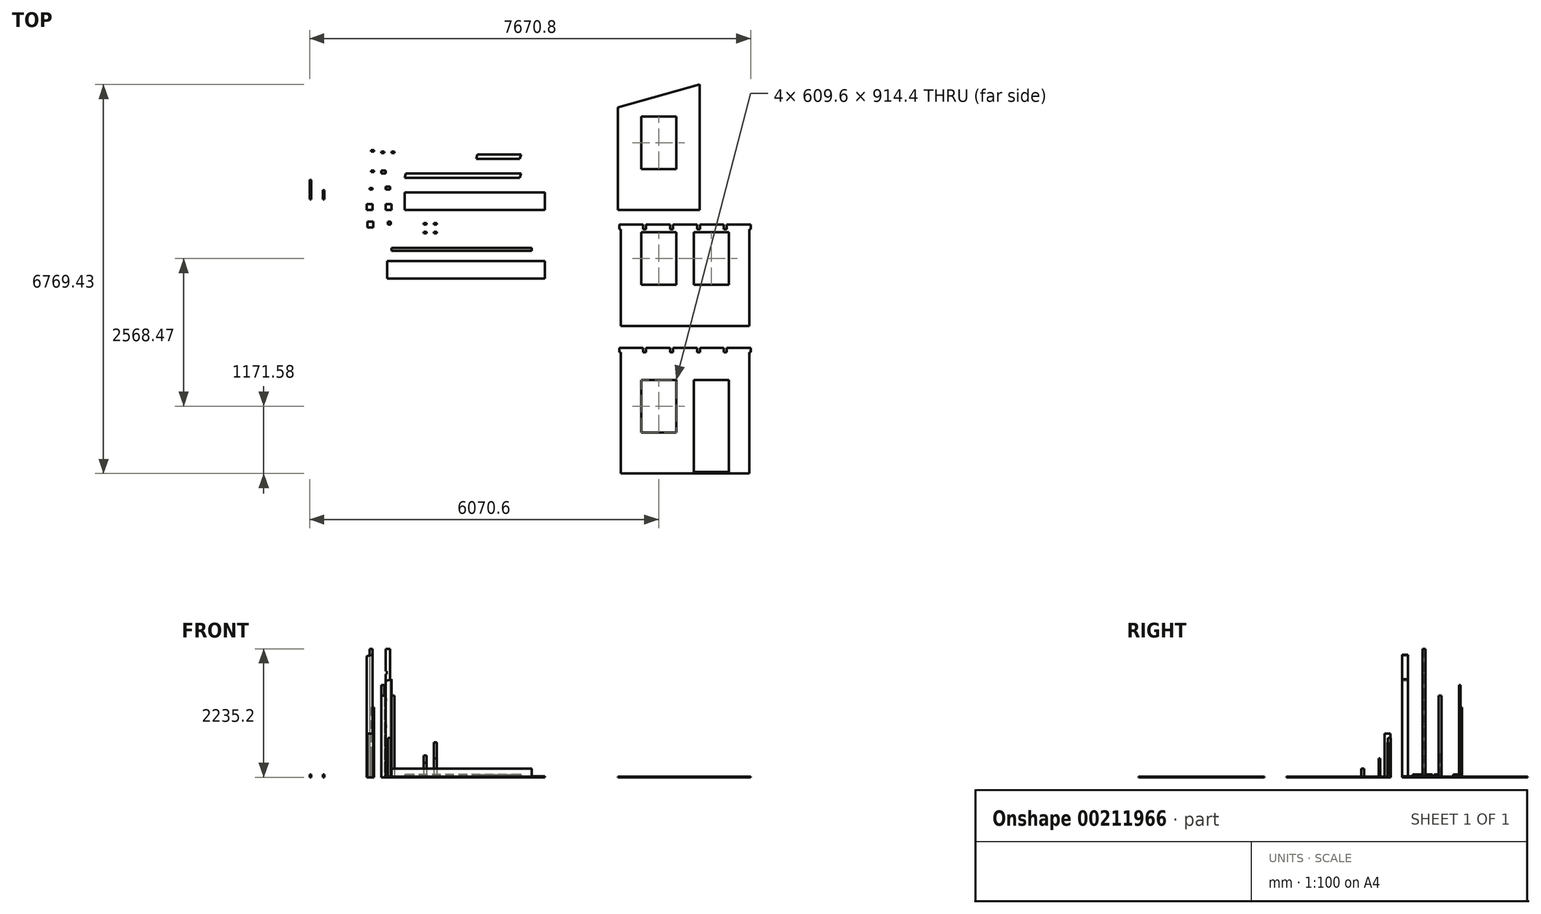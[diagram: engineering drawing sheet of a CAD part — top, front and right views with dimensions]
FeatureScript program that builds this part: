
annotation { "Feature Type Name" : "Feature", "Feature Type Description" : "" }
export const myFeature = defineFeature(function(context is Context, id is Id, definition is map)
    precondition{}
    {
        {
            var Q0;
            Q0=qCreatedBy(makeId("Front.planeOp"),FACE);
            var sketch = newSketch(context, id + "F0", { "sketchPlane" : qUnion([Q0])});
            skLineSegment(sketch, "E0", {"start": v(0, 0) * mm, "end": v(-304.8, 152.4) * mm});
            skLineSegment(sketch, "E1", {"start": v(-304.8, 152.4) * mm, "end": v(-304.8, 203.2) * mm});
            skLineSegment(sketch, "E2", {"start": v(-304.8, 203.2) * mm, "end": v(2133.6, 203.2) * mm});
            skLineSegment(sketch, "E3", {"start": v(2133.6, 203.2) * mm, "end": v(2133.6, 152.4) * mm});
            skLineSegment(sketch, "E4", {"start": v(2133.6, 152.4) * mm, "end": v(1828.8, 0) * mm});
            skLineSegment(sketch, "E5", {"start": v(1828.8, 0) * mm, "end": v(0, 0) * mm});
            skSolve(sketch);
        }
        {
            var Q0;
            Q0=makeQuery(id+"F0.imprint","IMPRINT",FACE,{"disambiguationData":[TD([[makeQuery(id+"F0.imprint","IMPRINT",EDGE,{"derivedFrom":sQuery(id+"F0.wireOp",EDGE,"E0")}),-1.0]])]});
            extrude(context, id + "F1", {"entities" : qUnion([Q0]), "depth" : 152.4 * mm});
        }
        {
            var Q0;
            Q0=qCreatedBy(makeId("Top.planeOp"),FACE);
            var sketch = newSketch(context, id + "F2", { "sketchPlane" : qUnion([Q0])});
            skLineSegment(sketch, "E6.bottom", {"start": v(-736.6, 355.6) * mm, "end": v(-635, 355.6) * mm});
            skLineSegment(sketch, "E6.top", {"start": v(-736.6, 254) * mm, "end": v(-635, 254) * mm});
            skLineSegment(sketch, "E6.left", {"start": v(-736.6, 355.6) * mm, "end": v(-736.6, 254) * mm});
            skLineSegment(sketch, "E6.right", {"start": v(-635, 355.6) * mm, "end": v(-635, 254) * mm});
            skSolve(sketch);
        }
        {
            var Q0;
            Q0=makeQuery(id+"F2.imprint","IMPRINT",FACE,{"disambiguationData":[TD([[makeQuery(id+"F2.imprint","IMPRINT",EDGE,{"derivedFrom":sQuery(id+"F2.wireOp",EDGE,"E6.bottom")}),-1.0]])]});
            extrude(context, id + "F3", {"entities" : qUnion([Q0]), "depth" : 2133.6 * mm});
        }
        {
            var Q0;
            Q0=makeQuery(id+"F3.opExtrude","SWEPT_FACE",FACE,{"disambiguationData":[OSD([sQuery(id+"F2.wireOp",EDGE,"E6.top")])]});
            var sketch = newSketch(context, id + "F4", { "sketchPlane" : qUnion([Q0])});
            skLineSegment(sketch, "E7", {"start": v(-736.6, 2133.6) * mm, "end": v(-736.6, 2105.03) * mm});
            skLineSegment(sketch, "E8", {"start": v(-736.6, 2105.03) * mm, "end": v(-635, 2133.6) * mm});
            skLineSegment(sketch, "E9", {"start": v(-635, 2133.6) * mm, "end": v(-736.6, 2133.6) * mm});
            skSolve(sketch);
        }
        {
            var Q0;
            Q0=makeQuery(id+"F4.imprint","IMPRINT",FACE,{"disambiguationData":[TD([[makeQuery(id+"F4.imprint","IMPRINT",EDGE,{"derivedFrom":sQuery(id+"F4.wireOp",EDGE,"E7")}),1.0]])]});
            extrude(context, id + "F5", {"entities" : qUnion([Q0]), "operationType" : NewBodyOperationType.REMOVE, "endBound" : BoundingType.UP_TO_NEXT, "oppositeDirection" : true, "depth" : 25.4 * mm});
        }
        {
            var Q0;
            Q0=qCreatedBy(makeId("Top.planeOp"),FACE);
            var sketch = newSketch(context, id + "F6", { "sketchPlane" : qUnion([Q0])});
            skLineSegment(sketch, "E10.bottom", {"start": v(-406.4, 355.6) * mm, "end": v(-304.8, 355.6) * mm});
            skLineSegment(sketch, "E10.top", {"start": v(-406.4, 254) * mm, "end": v(-304.8, 254) * mm});
            skLineSegment(sketch, "E10.left", {"start": v(-406.4, 355.6) * mm, "end": v(-406.4, 254) * mm});
            skLineSegment(sketch, "E10.right", {"start": v(-304.8, 355.6) * mm, "end": v(-304.8, 254) * mm});
            skSolve(sketch);
        }
        {
            var Q0;
            Q0=makeQuery(id+"F6.imprint","IMPRINT",FACE,{"disambiguationData":[TD([[makeQuery(id+"F6.imprint","IMPRINT",EDGE,{"derivedFrom":sQuery(id+"F6.wireOp",EDGE,"E10.bottom")}),-1.0]])]});
            extrude(context, id + "F7", {"entities" : qUnion([Q0]), "depth" : 1704.97 * mm});
        }
        {
            var Q0;
            Q0=makeQuery(id+"F7.opExtrude","SWEPT_FACE",FACE,{"disambiguationData":[OSD([sQuery(id+"F6.wireOp",EDGE,"E10.top")])]});
            var sketch = newSketch(context, id + "F8", { "sketchPlane" : qUnion([Q0])});
            skLineSegment(sketch, "E11", {"start": v(-406.4, 1704.98) * mm, "end": v(-406.4, 1676.4) * mm});
            skLineSegment(sketch, "E12", {"start": v(-406.4, 1676.4) * mm, "end": v(-304.8, 1704.98) * mm});
            skLineSegment(sketch, "E13", {"start": v(-304.8, 1704.98) * mm, "end": v(-406.4, 1704.98) * mm});
            skSolve(sketch);
        }
        {
            var Q0;
            Q0=makeQuery(id+"F8.imprint","IMPRINT",FACE,{"disambiguationData":[TD([[makeQuery(id+"F8.imprint","IMPRINT",EDGE,{"derivedFrom":sQuery(id+"F8.wireOp",EDGE,"E11")}),1.0]])]});
            extrude(context, id + "F9", {"entities" : qUnion([Q0]), "operationType" : NewBodyOperationType.REMOVE, "endBound" : BoundingType.UP_TO_NEXT, "oppositeDirection" : true, "depth" : 25.4 * mm});
        }
        {
            var Q0;
            Q0=qCreatedBy(makeId("Top.planeOp"),FACE);
            var sketch = newSketch(context, id + "F10", { "sketchPlane" : qUnion([Q0])});
            skLineSegment(sketch, "E14.bottom", {"start": v(-76.2, 254) * mm, "end": v(2362.2, 254) * mm});
            skLineSegment(sketch, "E14.top", {"start": v(-76.2, 558.8) * mm, "end": v(2362.2, 558.8) * mm});
            skLineSegment(sketch, "E14.left", {"start": v(-76.2, 254) * mm, "end": v(-76.2, 558.8) * mm});
            skLineSegment(sketch, "E14.right", {"start": v(2362.2, 254) * mm, "end": v(2362.2, 558.8) * mm});
            skSolve(sketch);
        }
        {
            var Q0;
            Q0=makeQuery(id+"F10.imprint","IMPRINT",FACE,{"disambiguationData":[TD([[makeQuery(id+"F10.imprint","IMPRINT",EDGE,{"derivedFrom":sQuery(id+"F10.wireOp",EDGE,"E14.bottom")}),1.0]])]});
            extrude(context, id + "F11", {"entities" : qUnion([Q0]), "depth" : 19.05 * mm});
        }
        {
            var Q0;
            Q0=qCreatedBy(makeId("Top.planeOp"),FACE);
            var sketch = newSketch(context, id + "F12", { "sketchPlane" : qUnion([Q0])});
            skLineSegment(sketch, "E15", {"start": v(-76.2, 812.8) * mm, "end": v(-54.35, 889) * mm});
            skLineSegment(sketch, "E16", {"start": v(-54.35, 889) * mm, "end": v(1950.98, 889) * mm});
            skLineSegment(sketch, "E17", {"start": v(1950.98, 889) * mm, "end": v(1929.13, 812.8) * mm});
            skLineSegment(sketch, "E18", {"start": v(1929.13, 812.8) * mm, "end": v(-76.2, 812.8) * mm});
            skSolve(sketch);
        }
        {
            var Q0;
            Q0=makeQuery(id+"F12.imprint","IMPRINT",FACE,{"disambiguationData":[TD([[makeQuery(id+"F12.imprint","IMPRINT",EDGE,{"derivedFrom":sQuery(id+"F12.wireOp",EDGE,"E15")}),-1.0]])]});
            extrude(context, id + "F13", {"entities" : qUnion([Q0]), "depth" : 50.8 * mm});
        }
        {
            var Q0;
            Q0=qCreatedBy(makeId("Top.planeOp"),FACE);
            var sketch = newSketch(context, id + "F14", { "sketchPlane" : qUnion([Q0])});
            skLineSegment(sketch, "E19.bottom", {"start": v(-406.4, 609.6) * mm, "end": v(-330.2, 609.6) * mm});
            skLineSegment(sketch, "E19.top", {"start": v(-406.4, 660.4) * mm, "end": v(-330.2, 660.4) * mm});
            skLineSegment(sketch, "E19.left", {"start": v(-406.4, 609.6) * mm, "end": v(-406.4, 660.4) * mm});
            skLineSegment(sketch, "E19.right", {"start": v(-330.2, 609.6) * mm, "end": v(-330.2, 660.4) * mm});
            skSolve(sketch);
        }
        {
            var Q0;
            Q0=makeQuery(id+"F14.imprint","IMPRINT",FACE,{"disambiguationData":[TD([[makeQuery(id+"F14.imprint","IMPRINT",EDGE,{"derivedFrom":sQuery(id+"F14.wireOp",EDGE,"E19.bottom")}),1.0]])]});
            extrude(context, id + "F15", {"entities" : qUnion([Q0]), "depth" : 2235.2 * mm});
        }
        {
            var Q0;
            Q0=qCreatedBy(makeId("Top.planeOp"),FACE);
            var sketch = newSketch(context, id + "F16", { "sketchPlane" : qUnion([Q0])});
            skLineSegment(sketch, "E20.bottom", {"start": v(-482.6, 939.8) * mm, "end": v(-406.4, 939.8) * mm});
            skLineSegment(sketch, "E20.top", {"start": v(-482.6, 889) * mm, "end": v(-406.4, 889) * mm});
            skLineSegment(sketch, "E20.left", {"start": v(-482.6, 939.8) * mm, "end": v(-482.6, 889) * mm});
            skLineSegment(sketch, "E20.right", {"start": v(-406.4, 939.8) * mm, "end": v(-406.4, 889) * mm});
            skSolve(sketch);
        }
        {
            var Q0;
            Q0=makeQuery(id+"F16.imprint","IMPRINT",FACE,{"disambiguationData":[TD([[makeQuery(id+"F16.imprint","IMPRINT",EDGE,{"derivedFrom":sQuery(id+"F16.wireOp",EDGE,"E20.bottom")}),-1.0]])]});
            extrude(context, id + "F17", {"entities" : qUnion([Q0]), "depth" : 1422.4 * mm});
        }
        {
            var Q0;
            Q0=makeQuery(id+"F15.opExtrude","SWEPT_FACE",FACE,{"disambiguationData":[OSD([sQuery(id+"F14.wireOp",EDGE,"E19.top")])]});
            var sketch = newSketch(context, id + "F18", { "sketchPlane" : qUnion([Q0])});
            skLineSegment(sketch, "E21", {"start": v(406.4, 1844.04) * mm, "end": v(384.8, 1844.04) * mm});
            skLineSegment(sketch, "E22", {"start": v(384.8, 1844.04) * mm, "end": v(384.8, 1793.24) * mm});
            skLineSegment(sketch, "E23", {"start": v(384.8, 1793.24) * mm, "end": v(406.4, 1793.24) * mm});
            skLineSegment(sketch, "E24.bottom", {"start": v(406.4, 1376.68) * mm, "end": v(384.81, 1376.68) * mm});
            skLineSegment(sketch, "E24.top", {"start": v(406.4, 1325.88) * mm, "end": v(384.81, 1325.88) * mm});
            skLineSegment(sketch, "E24.left", {"start": v(406.4, 1376.68) * mm, "end": v(406.4, 1325.88) * mm});
            skLineSegment(sketch, "E24.right", {"start": v(384.81, 1376.68) * mm, "end": v(384.81, 1325.88) * mm});
            skLineSegment(sketch, "E25.bottom", {"start": v(406.4, 858.52) * mm, "end": v(384.81, 858.52) * mm});
            skLineSegment(sketch, "E26.top", {"start": v(406.4, 909.32) * mm, "end": v(384.81, 909.32) * mm});
            skLineSegment(sketch, "E27.bottom", {"start": v(406.4, 441.96) * mm, "end": v(384.81, 441.96) * mm});
            skLineSegment(sketch, "E27.top", {"start": v(406.4, 391.16) * mm, "end": v(384.81, 391.16) * mm});
            skLineSegment(sketch, "E27.left", {"start": v(406.4, 441.96) * mm, "end": v(406.4, 391.16) * mm});
            skLineSegment(sketch, "E27.right", {"start": v(384.81, 441.96) * mm, "end": v(384.81, 391.16) * mm});
            skLineSegment(sketch, "E28", {"start": v(406.4, 909.32) * mm, "end": v(406.4, 858.52) * mm});
            skLineSegment(sketch, "E29", {"start": v(384.81, 909.32) * mm, "end": v(384.81, 858.52) * mm});
            skSolve(sketch);
        }
        {
            var Q0;
            {var subQ0=sQuery(id+"F18.wireOp",EDGE,"E21");Q0=makeQuery(id+"F18.imprint","IMPRINT",FACE,{"disambiguationData":[TD([[makeQuery(id+"F18.imprint","IMPRINT",EDGE,{"derivedFrom":subQ0}),1.0]])]});}
            var Q1;
            Q1=makeQuery(id+"F18.imprint","IMPRINT",FACE,{"disambiguationData":[TD([[makeQuery(id+"F18.imprint","IMPRINT",EDGE,{"derivedFrom":sQuery(id+"F18.wireOp",EDGE,"E24.bottom")}),1.0]])]});
            var Q2;
            Q2=makeQuery(id+"F18.imprint","IMPRINT",FACE,{"disambiguationData":[TD([[makeQuery(id+"F18.imprint","IMPRINT",EDGE,{"derivedFrom":sQuery(id+"F18.wireOp",EDGE,"E25.bottom")}),-1.0]])]});
            var Q3;
            Q3=makeQuery(id+"F18.imprint","IMPRINT",FACE,{"disambiguationData":[TD([[makeQuery(id+"F18.imprint","IMPRINT",EDGE,{"derivedFrom":sQuery(id+"F18.wireOp",EDGE,"E27.bottom")}),1.0]])]});
            extrude(context, id + "F19", {"entities" : qUnion([Q0, Q1, Q2, Q3]), "operationType" : NewBodyOperationType.REMOVE, "endBound" : BoundingType.UP_TO_NEXT, "oppositeDirection" : true, "depth" : 25.4 * mm});
        }
        {
            var Q0;
            Q0=qCreatedBy(makeId("Top.planeOp"),FACE);
            var sketch = newSketch(context, id + "F20", { "sketchPlane" : qUnion([Q0])});
            skLineSegment(sketch, "E30.bottom", {"start": v(-685.8, 609.6) * mm, "end": v(-635, 609.6) * mm});
            skLineSegment(sketch, "E30.top", {"start": v(-685.8, 635) * mm, "end": v(-635, 635) * mm});
            skLineSegment(sketch, "E30.left", {"start": v(-685.8, 609.6) * mm, "end": v(-685.8, 635) * mm});
            skLineSegment(sketch, "E30.right", {"start": v(-635, 609.6) * mm, "end": v(-635, 635) * mm});
            skSolve(sketch);
        }
        {
            var Q0;
            Q0=makeQuery(id+"F20.imprint","IMPRINT",FACE,{"disambiguationData":[TD([[makeQuery(id+"F20.imprint","IMPRINT",EDGE,{"derivedFrom":sQuery(id+"F20.wireOp",EDGE,"E30.bottom")}),1.0]])]});
            extrude(context, id + "F21", {"entities" : qUnion([Q0]), "depth" : 2235.2 * mm});
        }
        {
            var Q0;
            Q0=qCreatedBy(makeId("Top.planeOp"),FACE);
            var sketch = newSketch(context, id + "F22", { "sketchPlane" : qUnion([Q0])});
            skLineSegment(sketch, "E31.bottom", {"start": v(-660.4, 889) * mm, "end": v(-609.6, 889) * mm});
            skLineSegment(sketch, "E31.top", {"start": v(-660.4, 863.6) * mm, "end": v(-609.6, 863.6) * mm});
            skLineSegment(sketch, "E31.left", {"start": v(-660.4, 889) * mm, "end": v(-660.4, 863.6) * mm});
            skLineSegment(sketch, "E31.right", {"start": v(-609.6, 889) * mm, "end": v(-609.6, 863.6) * mm});
            skSolve(sketch);
        }
        {
            var Q0;
            Q0=makeQuery(id+"F22.imprint","IMPRINT",FACE,{"disambiguationData":[TD([[makeQuery(id+"F22.imprint","IMPRINT",EDGE,{"derivedFrom":sQuery(id+"F22.wireOp",EDGE,"E31.bottom")}),-1.0]])]});
            extrude(context, id + "F23", {"entities" : qUnion([Q0]), "depth" : 1628.77 * mm});
        }
        {
            var Q0;
            Q0=qCreatedBy(makeId("Top.planeOp"),FACE);
            var sketch = newSketch(context, id + "F24", { "sketchPlane" : qUnion([Q0])});
            skLineSegment(sketch, "E32.bottom", {"start": v(-660.4, 1295.4) * mm, "end": v(-609.6, 1295.4) * mm});
            skLineSegment(sketch, "E32.top", {"start": v(-660.4, 1270) * mm, "end": v(-609.6, 1270) * mm});
            skLineSegment(sketch, "E32.left", {"start": v(-660.4, 1295.4) * mm, "end": v(-660.4, 1270) * mm});
            skLineSegment(sketch, "E32.right", {"start": v(-609.6, 1295.4) * mm, "end": v(-609.6, 1270) * mm});
            skSolve(sketch);
        }
        {
            var Q0;
            Q0=makeQuery(id+"F24.imprint","IMPRINT",FACE,{"disambiguationData":[TD([[makeQuery(id+"F24.imprint","IMPRINT",EDGE,{"derivedFrom":sQuery(id+"F24.wireOp",EDGE,"E32.bottom")}),-1.0]])]});
            extrude(context, id + "F25", {"entities" : qUnion([Q0]), "depth" : 1219.2 * mm});
        }
        {
            var Q0;
            Q0=qCreatedBy(makeId("Top.planeOp"),FACE);
            var sketch = newSketch(context, id + "F26", { "sketchPlane" : qUnion([Q0])});
            skLineSegment(sketch, "E33.bottom", {"start": v(-482.6, 1270) * mm, "end": v(-431.8, 1270) * mm});
            skLineSegment(sketch, "E33.top", {"start": v(-482.6, 1244.6) * mm, "end": v(-431.8, 1244.6) * mm});
            skLineSegment(sketch, "E33.left", {"start": v(-482.6, 1270) * mm, "end": v(-482.6, 1244.6) * mm});
            skLineSegment(sketch, "E33.right", {"start": v(-431.8, 1270) * mm, "end": v(-431.8, 1244.6) * mm});
            skSolve(sketch);
        }
        {
            var Q0;
            Q0=makeQuery(id+"F26.imprint","IMPRINT",FACE,{"disambiguationData":[TD([[makeQuery(id+"F26.imprint","IMPRINT",EDGE,{"derivedFrom":sQuery(id+"F26.wireOp",EDGE,"E33.bottom")}),-1.0]])]});
            extrude(context, id + "F27", {"entities" : qUnion([Q0]), "depth" : 1603.38 * mm});
        }
        {
            var Q0;
            Q0=qCreatedBy(makeId("Top.planeOp"),FACE);
            var sketch = newSketch(context, id + "F28", { "sketchPlane" : qUnion([Q0])});
            skLineSegment(sketch, "E34.bottom", {"start": v(-254, 1270) * mm, "end": v(-304.8, 1270) * mm});
            skLineSegment(sketch, "E34.top", {"start": v(-254, 1244.6) * mm, "end": v(-304.8, 1244.6) * mm});
            skLineSegment(sketch, "E34.left", {"start": v(-254, 1270) * mm, "end": v(-254, 1244.6) * mm});
            skLineSegment(sketch, "E34.right", {"start": v(-304.8, 1270) * mm, "end": v(-304.8, 1244.6) * mm});
            skSolve(sketch);
        }
        {
            var Q0;
            Q0=makeQuery(id+"F28.imprint","IMPRINT",FACE,{"disambiguationData":[TD([[makeQuery(id+"F28.imprint","IMPRINT",EDGE,{"derivedFrom":sQuery(id+"F28.wireOp",EDGE,"E34.bottom")}),1.0]])]});
            extrude(context, id + "F29", {"entities" : qUnion([Q0]), "depth" : 1422.4 * mm});
        }
        {
            var Q0;
            Q0=qCreatedBy(makeId("Top.planeOp"),FACE);
            var sketch = newSketch(context, id + "F30", { "sketchPlane" : qUnion([Q0])});
            skLineSegment(sketch, "E35", {"start": v(1950.98, 1219.2) * mm, "end": v(1929.13, 1143) * mm});
            skLineSegment(sketch, "E36", {"start": v(1929.13, 1143) * mm, "end": v(1167.13, 1143) * mm});
            skLineSegment(sketch, "E37", {"start": v(1167.13, 1143) * mm, "end": v(1188.98, 1219.2) * mm});
            skLineSegment(sketch, "E38", {"start": v(1188.98, 1219.2) * mm, "end": v(1950.98, 1219.2) * mm});
            skSolve(sketch);
        }
        {
            var Q0;
            Q0=makeQuery(id+"F30.imprint","IMPRINT",FACE,{"disambiguationData":[TD([[makeQuery(id+"F30.imprint","IMPRINT",EDGE,{"derivedFrom":sQuery(id+"F30.wireOp",EDGE,"E35")}),-1.0]])]});
            extrude(context, id + "F31", {"entities" : qUnion([Q0]), "depth" : 50.8 * mm});
        }
        {
            var Q0;
            Q0=qCreatedBy(makeId("Top.planeOp"),FACE);
            var sketch = newSketch(context, id + "F32", { "sketchPlane" : qUnion([Q0])});
            skLineSegment(sketch, "E39.bottom", {"start": v(2133.6, -406.4) * mm, "end": v(-304.8, -406.4) * mm});
            skLineSegment(sketch, "E39.top", {"start": v(2133.6, -457.2) * mm, "end": v(-304.8, -457.2) * mm});
            skLineSegment(sketch, "E39.left", {"start": v(2133.6, -406.4) * mm, "end": v(2133.6, -457.2) * mm});
            skLineSegment(sketch, "E39.right", {"start": v(-304.8, -406.4) * mm, "end": v(-304.8, -457.2) * mm});
            skSolve(sketch);
        }
        {
            var Q0;
            Q0=makeQuery(id+"F32.imprint","IMPRINT",FACE,{"disambiguationData":[TD([[makeQuery(id+"F32.imprint","IMPRINT",EDGE,{"derivedFrom":sQuery(id+"F32.wireOp",EDGE,"E39.bottom")}),1.0]])]});
            extrude(context, id + "F33", {"entities" : qUnion([Q0]), "depth" : 152.4 * mm});
        }
        {
            var Q0;
            Q0=makeQuery(id+"F23.opExtrude","SWEPT_BODY",BODY,{"disambiguationData":[OSD([sQuery(id+"F22.wireOp",EDGE,"E31.bottom"),sQuery(id+"F22.wireOp",EDGE,"E31.top"),sQuery(id+"F22.wireOp",EDGE,"E31.left"),sQuery(id+"F22.wireOp",EDGE,"E31.right")])]});
            deleteBodies(context, id + "F34", {"entities" : qUnion([Q0])});
        }
        {
            var Q0;
            Q0=makeQuery(id+"F1.opExtrude","SWEPT_BODY",BODY,{"disambiguationData":[OSD([sQuery(id+"F0.wireOp",EDGE,"E0"),sQuery(id+"F0.wireOp",EDGE,"E1"),sQuery(id+"F0.wireOp",EDGE,"E2"),sQuery(id+"F0.wireOp",EDGE,"E3"),sQuery(id+"F0.wireOp",EDGE,"E4"),sQuery(id+"F0.wireOp",EDGE,"E5")])]});
            deleteBodies(context, id + "F35", {"entities" : qUnion([Q0])});
        }
        {
            var Q0;
            Q0=qCreatedBy(makeId("Top.planeOp"),FACE);
            var sketch = newSketch(context, id + "F36", { "sketchPlane" : qUnion([Q0])});
            skLineSegment(sketch, "E40.bottom", {"start": v(254, 25.4) * mm, "end": v(304.8, 25.4) * mm});
            skLineSegment(sketch, "E40.top", {"start": v(254, 0) * mm, "end": v(304.8, 0) * mm});
            skLineSegment(sketch, "E40.left", {"start": v(254, 25.4) * mm, "end": v(254, 0) * mm});
            skLineSegment(sketch, "E40.right", {"start": v(304.8, 25.4) * mm, "end": v(304.8, 0) * mm});
            skSolve(sketch);
        }
        {
            var Q0;
            Q0=makeQuery(id+"F36.imprint","IMPRINT",FACE,{"disambiguationData":[TD([[makeQuery(id+"F36.imprint","IMPRINT",EDGE,{"derivedFrom":sQuery(id+"F36.wireOp",EDGE,"E40.bottom")}),-1.0]])]});
            extrude(context, id + "F37", {"entities" : qUnion([Q0]), "depth" : 381 * mm});
        }
        {
            var Q0;
            Q0=qCreatedBy(makeId("Top.planeOp"),FACE);
            var sketch = newSketch(context, id + "F38", { "sketchPlane" : qUnion([Q0])});
            skLineSegment(sketch, "E41.bottom", {"start": v(431.8, 25.4) * mm, "end": v(482.6, 25.4) * mm});
            skLineSegment(sketch, "E41.top", {"start": v(431.8, 0) * mm, "end": v(482.6, 0) * mm});
            skLineSegment(sketch, "E41.left", {"start": v(431.8, 25.4) * mm, "end": v(431.8, 0) * mm});
            skLineSegment(sketch, "E41.right", {"start": v(482.6, 25.4) * mm, "end": v(482.6, 0) * mm});
            skSolve(sketch);
        }
        {
            var Q0;
            Q0=makeQuery(id+"F38.imprint","IMPRINT",FACE,{"disambiguationData":[TD([[makeQuery(id+"F38.imprint","IMPRINT",EDGE,{"derivedFrom":sQuery(id+"F38.wireOp",EDGE,"E41.bottom")}),-1.0]])]});
            extrude(context, id + "F39", {"entities" : qUnion([Q0]), "depth" : 609.6 * mm});
        }
        {
            var Q0;
            Q0=qCreatedBy(makeId("Top.planeOp"),FACE);
            var sketch = newSketch(context, id + "F40", { "sketchPlane" : qUnion([Q0])});
            skLineSegment(sketch, "E42.bottom", {"start": v(254, -127) * mm, "end": v(304.8, -127) * mm});
            skLineSegment(sketch, "E42.top", {"start": v(254, -152.4) * mm, "end": v(304.8, -152.4) * mm});
            skLineSegment(sketch, "E42.left", {"start": v(254, -127) * mm, "end": v(254, -152.4) * mm});
            skLineSegment(sketch, "E42.right", {"start": v(304.8, -127) * mm, "end": v(304.8, -152.4) * mm});
            skSolve(sketch);
        }
        {
            var Q0;
            Q0=makeQuery(id+"F40.imprint","IMPRINT",FACE,{"disambiguationData":[TD([[makeQuery(id+"F40.imprint","IMPRINT",EDGE,{"derivedFrom":sQuery(id+"F40.wireOp",EDGE,"E42.bottom")}),-1.0]])]});
            extrude(context, id + "F41", {"entities" : qUnion([Q0]), "depth" : 254 * mm});
        }
        {
            var Q0;
            Q0=qCreatedBy(makeId("Top.planeOp"),FACE);
            var sketch = newSketch(context, id + "F42", { "sketchPlane" : qUnion([Q0])});
            skLineSegment(sketch, "E43.bottom", {"start": v(431.8, -127) * mm, "end": v(482.6, -127) * mm});
            skLineSegment(sketch, "E43.top", {"start": v(431.8, -152.4) * mm, "end": v(482.6, -152.4) * mm});
            skLineSegment(sketch, "E43.left", {"start": v(431.8, -127) * mm, "end": v(431.8, -152.4) * mm});
            skLineSegment(sketch, "E43.right", {"start": v(482.6, -127) * mm, "end": v(482.6, -152.4) * mm});
            skSolve(sketch);
        }
        {
            var Q0;
            Q0=makeQuery(id+"F42.imprint","IMPRINT",FACE,{"disambiguationData":[TD([[makeQuery(id+"F42.imprint","IMPRINT",EDGE,{"derivedFrom":sQuery(id+"F42.wireOp",EDGE,"E43.bottom")}),-1.0]])]});
            extrude(context, id + "F43", {"entities" : qUnion([Q0]), "depth" : 330.2 * mm});
        }
        {
            var Q0;
            Q0=qCreatedBy(makeId("Top.planeOp"),FACE);
            var sketch = newSketch(context, id + "F44", { "sketchPlane" : qUnion([Q0])});
            skLineSegment(sketch, "E44.bottom", {"start": v(-381, -635) * mm, "end": v(2362.2, -635) * mm});
            skLineSegment(sketch, "E44.top", {"start": v(-381, -939.8) * mm, "end": v(2362.2, -939.8) * mm});
            skLineSegment(sketch, "E44.left", {"start": v(-381, -635) * mm, "end": v(-381, -939.8) * mm});
            skLineSegment(sketch, "E44.right", {"start": v(2362.2, -635) * mm, "end": v(2362.2, -939.8) * mm});
            skSolve(sketch);
        }
        {
            var Q0;
            Q0=makeQuery(id+"F44.imprint","IMPRINT",FACE,{"disambiguationData":[TD([[makeQuery(id+"F44.imprint","IMPRINT",EDGE,{"derivedFrom":sQuery(id+"F44.wireOp",EDGE,"E44.bottom")}),-1.0]])]});
            extrude(context, id + "F45", {"entities" : qUnion([Q0]), "depth" : 12.7 * mm});
        }
        {
            var Q0;
            Q0=qCreatedBy(makeId("Top.planeOp"),FACE);
            var sketch = newSketch(context, id + "F46", { "sketchPlane" : qUnion([Q0])});
            skLineSegment(sketch, "E45", {"start": v(3632.2, 254) * mm, "end": v(5054.6, 254) * mm});
            skLineSegment(sketch, "E46", {"start": v(5054.6, 254) * mm, "end": v(5054.6, 2438.3) * mm});
            skLineSegment(sketch, "E47", {"start": v(5054.6, 2438.3) * mm, "end": v(3632.2, 2038.12) * mm});
            skLineSegment(sketch, "E48", {"start": v(3632.2, 2038.12) * mm, "end": v(3632.2, 254) * mm});
            skSolve(sketch);
        }
        {
            var Q0;
            Q0=makeQuery(id+"F46.imprint","IMPRINT",FACE,{"disambiguationData":[TD([[makeQuery(id+"F46.imprint","IMPRINT",EDGE,{"derivedFrom":sQuery(id+"F46.wireOp",EDGE,"E45")}),1.0]])]});
            extrude(context, id + "F47", {"entities" : qUnion([Q0]), "depth" : 9 * mm});
        }
        {
            var Q0;
            Q0=makeQuery(id+"F47.opExtrude","CAP_FACE",FACE,{"disambiguationData":[OSD([sQuery(id+"F46.wireOp",EDGE,"E45"),sQuery(id+"F46.wireOp",EDGE,"E46"),sQuery(id+"F46.wireOp",EDGE,"E47"),sQuery(id+"F46.wireOp",EDGE,"E48")])],"isStart":false});
            var sketch = newSketch(context, id + "F48", { "sketchPlane" : qUnion([Q0])});
            skLineSegment(sketch, "E49.bottom", {"start": v(4038.6, 1882.77) * mm, "end": v(4648.2, 1882.77) * mm});
            skLineSegment(sketch, "E49.top", {"start": v(4038.6, 968.37) * mm, "end": v(4648.2, 968.37) * mm});
            skLineSegment(sketch, "E49.left", {"start": v(4038.6, 1882.77) * mm, "end": v(4038.6, 968.37) * mm});
            skLineSegment(sketch, "E49.right", {"start": v(4648.2, 1882.77) * mm, "end": v(4648.2, 968.37) * mm});
            skSolve(sketch);
        }
        {
            var Q0;
            Q0=makeQuery(id+"F48.imprint","IMPRINT",FACE,{"disambiguationData":[TD([[makeQuery(id+"F48.imprint","IMPRINT",EDGE,{"derivedFrom":sQuery(id+"F48.wireOp",EDGE,"E49.bottom")}),-1.0]])]});
            extrude(context, id + "F49", {"entities" : qUnion([Q0]), "operationType" : NewBodyOperationType.REMOVE, "endBound" : BoundingType.UP_TO_NEXT, "oppositeDirection" : true, "depth" : 25.4 * mm});
        }
        {
            var Q0;
            Q0=qCreatedBy(makeId("Top.planeOp"),FACE);
            var sketch = newSketch(context, id + "F50", { "sketchPlane" : qUnion([Q0])});
            skLineSegment(sketch, "E50.bottom", {"start": v(-660.4, 939.8) * mm, "end": v(-609.6, 939.8) * mm});
            skLineSegment(sketch, "E50.top", {"start": v(-660.4, 914.4) * mm, "end": v(-609.6, 914.4) * mm});
            skLineSegment(sketch, "E50.left", {"start": v(-660.4, 939.8) * mm, "end": v(-660.4, 914.4) * mm});
            skLineSegment(sketch, "E50.right", {"start": v(-609.6, 939.8) * mm, "end": v(-609.6, 914.4) * mm});
            skSolve(sketch);
        }
        {
            var Q0;
            Q0=makeQuery(id+"F50.imprint","IMPRINT",FACE,{"disambiguationData":[TD([[makeQuery(id+"F50.imprint","IMPRINT",EDGE,{"derivedFrom":sQuery(id+"F50.wireOp",EDGE,"E50.bottom")}),-1.0]])]});
            extrude(context, id + "F51", {"entities" : qUnion([Q0]), "depth" : 403.22 * mm});
        }
        {
            var Q0;
            Q0=qCreatedBy(makeId("Top.planeOp"),FACE);
            var sketch = newSketch(context, id + "F52", { "sketchPlane" : qUnion([Q0])});
            skLineSegment(sketch, "E51", {"start": v(-1727.2, 782.11) * mm, "end": v(-1727.2, 438.42) * mm});
            skLineSegment(sketch, "E52", {"start": v(-1727.2, 438.42) * mm, "end": v(-1701.8, 438.42) * mm});
            skLineSegment(sketch, "E53", {"start": v(-1701.8, 438.42) * mm, "end": v(-1701.8, 774.97) * mm});
            skLineSegment(sketch, "E54", {"start": v(-1701.8, 774.97) * mm, "end": v(-1727.2, 782.11) * mm});
            skLineSegment(sketch, "E55", {"start": v(-1498.6, 438.42) * mm, "end": v(-1473.2, 438.42) * mm});
            skLineSegment(sketch, "E56", {"start": v(-1473.2, 438.42) * mm, "end": v(-1473.2, 596.38) * mm});
            skLineSegment(sketch, "E57", {"start": v(-1473.2, 596.38) * mm, "end": v(-1498.6, 603.52) * mm});
            skLineSegment(sketch, "E58", {"start": v(-1498.6, 603.52) * mm, "end": v(-1498.6, 438.42) * mm});
            skSolve(sketch);
        }
        {
            var Q0;
            Q0=makeQuery(id+"F52.imprint","IMPRINT",FACE,{"disambiguationData":[TD([[makeQuery(id+"F52.imprint","IMPRINT",EDGE,{"derivedFrom":sQuery(id+"F52.wireOp",EDGE,"E51")}),1.0]])]});
            extrude(context, id + "F53", {"entities" : qUnion([Q0]), "depth" : 50.8 * mm});
        }
        {
            var Q0;
            Q0 = qSketchRegion(id + "F52", true);
            extrude(context, id + "F54", {"entities" : qUnion([Q0]), "operationType" : NewBodyOperationType.ADD, "depth" : 50.8 * mm});
        }
        {
            var Q0;
            Q0=qCreatedBy(makeId("Top.planeOp"),FACE);
            var sketch = newSketch(context, id + "F55", { "sketchPlane" : qUnion([Q0])});
            skLineSegment(sketch, "E59", {"start": v(3657.6, 0) * mm, "end": v(3657.6, -79.27) * mm});
            skLineSegment(sketch, "E60", {"start": v(3657.6, -79.27) * mm, "end": v(3683, -79.27) * mm});
            skLineSegment(sketch, "E61", {"start": v(3683, -79.27) * mm, "end": v(3683, -1762.66) * mm});
            skLineSegment(sketch, "E62", {"start": v(3683, -1762.66) * mm, "end": v(5918.2, -1762.66) * mm});
            skLineSegment(sketch, "E63", {"start": v(5918.2, -1762.66) * mm, "end": v(5918.2, -79.27) * mm});
            skLineSegment(sketch, "E64", {"start": v(5918.2, -79.27) * mm, "end": v(5943.6, -79.27) * mm});
            skLineSegment(sketch, "E65", {"start": v(5943.6, -79.27) * mm, "end": v(5943.6, 0) * mm});
            skLineSegment(sketch, "E66", {"start": v(5943.6, 0) * mm, "end": v(5527.04, 0) * mm});
            skLineSegment(sketch, "E67", {"start": v(5527.04, 0) * mm, "end": v(5527.04, -79.27) * mm});
            skLineSegment(sketch, "E68", {"start": v(5527.04, -79.27) * mm, "end": v(5476.24, -79.27) * mm});
            skLineSegment(sketch, "E69", {"start": v(5476.24, -79.27) * mm, "end": v(5476.24, 0) * mm});
            skLineSegment(sketch, "E70", {"start": v(5476.24, 0) * mm, "end": v(5059.68, 0) * mm});
            skLineSegment(sketch, "E71", {"start": v(5059.68, 0) * mm, "end": v(5059.68, -79.27) * mm});
            skLineSegment(sketch, "E72", {"start": v(5059.68, -79.27) * mm, "end": v(5008.88, -79.27) * mm});
            skLineSegment(sketch, "E73", {"start": v(5008.88, -79.27) * mm, "end": v(5008.88, 0) * mm});
            skLineSegment(sketch, "E74", {"start": v(5008.88, 0) * mm, "end": v(4592.32, 0) * mm});
            skLineSegment(sketch, "E75", {"start": v(4592.32, 0) * mm, "end": v(4592.32, -79.27) * mm});
            skLineSegment(sketch, "E76", {"start": v(4592.32, -79.27) * mm, "end": v(4541.52, -79.27) * mm});
            skLineSegment(sketch, "E77", {"start": v(4541.52, -79.27) * mm, "end": v(4541.52, 0) * mm});
            skLineSegment(sketch, "E78", {"start": v(4541.52, 0) * mm, "end": v(4124.96, 0) * mm});
            skLineSegment(sketch, "E79", {"start": v(4124.96, 0) * mm, "end": v(4124.96, -79.27) * mm});
            skLineSegment(sketch, "E80", {"start": v(4124.96, -79.27) * mm, "end": v(4074.16, -79.27) * mm});
            skLineSegment(sketch, "E81", {"start": v(4074.16, -79.27) * mm, "end": v(4074.16, 0) * mm});
            skLineSegment(sketch, "E82", {"start": v(4074.16, 0) * mm, "end": v(3657.6, 0) * mm});
            skSolve(sketch);
        }
        {
            var Q0;
            Q0=makeQuery(id+"F55.imprint","IMPRINT",FACE,{"disambiguationData":[TD([[makeQuery(id+"F55.imprint","IMPRINT",EDGE,{"derivedFrom":sQuery(id+"F55.wireOp",EDGE,"E59")}),1.0]])]});
            extrude(context, id + "F56", {"entities" : qUnion([Q0]), "depth" : 9 * mm});
        }
        {
            var Q0;
            Q0=makeQuery(id+"F56.opExtrude","CAP_FACE",FACE,{"disambiguationData":[OSD([sQuery(id+"F55.wireOp",EDGE,"E59"),sQuery(id+"F55.wireOp",EDGE,"E60"),sQuery(id+"F55.wireOp",EDGE,"E61"),sQuery(id+"F55.wireOp",EDGE,"E62"),sQuery(id+"F55.wireOp",EDGE,"E63"),sQuery(id+"F55.wireOp",EDGE,"E64"),sQuery(id+"F55.wireOp",EDGE,"E65"),sQuery(id+"F55.wireOp",EDGE,"E66"),sQuery(id+"F55.wireOp",EDGE,"E67"),sQuery(id+"F55.wireOp",EDGE,"E68"),sQuery(id+"F55.wireOp",EDGE,"E69"),sQuery(id+"F55.wireOp",EDGE,"E70"),sQuery(id+"F55.wireOp",EDGE,"E71"),sQuery(id+"F55.wireOp",EDGE,"E72"),sQuery(id+"F55.wireOp",EDGE,"E73"),sQuery(id+"F55.wireOp",EDGE,"E74"),sQuery(id+"F55.wireOp",EDGE,"E75"),sQuery(id+"F55.wireOp",EDGE,"E76"),sQuery(id+"F55.wireOp",EDGE,"E77"),sQuery(id+"F55.wireOp",EDGE,"E78"),sQuery(id+"F55.wireOp",EDGE,"E79"),sQuery(id+"F55.wireOp",EDGE,"E80"),sQuery(id+"F55.wireOp",EDGE,"E81"),sQuery(id+"F55.wireOp",EDGE,"E82")])],"isStart":false});
            var sketch = newSketch(context, id + "F57", { "sketchPlane" : qUnion([Q0])});
            skLineSegment(sketch, "E83.bottom", {"start": v(4038.6, -133.88) * mm, "end": v(4648.2, -133.88) * mm});
            skLineSegment(sketch, "E83.top", {"start": v(4038.6, -1048.28) * mm, "end": v(4648.2, -1048.28) * mm});
            skLineSegment(sketch, "E83.left", {"start": v(4038.6, -133.88) * mm, "end": v(4038.6, -1048.28) * mm});
            skLineSegment(sketch, "E83.right", {"start": v(4648.2, -133.88) * mm, "end": v(4648.2, -1048.28) * mm});
            skLineSegment(sketch, "E84.bottom", {"start": v(4953, -133.88) * mm, "end": v(5562.6, -133.88) * mm});
            skLineSegment(sketch, "E84.top", {"start": v(4953, -1048.28) * mm, "end": v(5562.6, -1048.28) * mm});
            skLineSegment(sketch, "E84.left", {"start": v(4953, -133.88) * mm, "end": v(4953, -1048.28) * mm});
            skLineSegment(sketch, "E84.right", {"start": v(5562.6, -133.88) * mm, "end": v(5562.6, -1048.28) * mm});
            skSolve(sketch);
        }
        {
            var Q0;
            Q0=makeQuery(id+"F57.imprint","IMPRINT",FACE,{"disambiguationData":[TD([[makeQuery(id+"F57.imprint","IMPRINT",EDGE,{"derivedFrom":sQuery(id+"F57.wireOp",EDGE,"E83.bottom")}),-1.0]])]});
            var Q1;
            Q1=makeQuery(id+"F57.imprint","IMPRINT",FACE,{"disambiguationData":[TD([[makeQuery(id+"F57.imprint","IMPRINT",EDGE,{"derivedFrom":sQuery(id+"F57.wireOp",EDGE,"E84.bottom")}),-1.0]])]});
            extrude(context, id + "F58", {"entities" : qUnion([Q0, Q1]), "operationType" : NewBodyOperationType.REMOVE, "endBound" : BoundingType.UP_TO_NEXT, "oppositeDirection" : true, "depth" : 25.4 * mm});
        }
        {
            var Q0;
            Q0=qCreatedBy(makeId("Top.planeOp"),FACE);
            var sketch = newSketch(context, id + "F59", { "sketchPlane" : qUnion([Q0])});
            skLineSegment(sketch, "E85", {"start": v(3657.6, -2143.66) * mm, "end": v(4074.16, -2143.66) * mm});
            skLineSegment(sketch, "E86", {"start": v(4074.16, -2143.66) * mm, "end": v(4074.16, -2222.93) * mm});
            skLineSegment(sketch, "E87", {"start": v(4074.16, -2222.93) * mm, "end": v(4124.96, -2222.93) * mm});
            skLineSegment(sketch, "E88", {"start": v(4124.96, -2222.93) * mm, "end": v(4124.96, -2143.66) * mm});
            skLineSegment(sketch, "E89", {"start": v(4124.96, -2143.66) * mm, "end": v(4541.52, -2143.66) * mm});
            skLineSegment(sketch, "E90", {"start": v(4541.52, -2143.66) * mm, "end": v(4541.52, -2222.93) * mm});
            skLineSegment(sketch, "E91", {"start": v(4541.52, -2222.93) * mm, "end": v(4592.32, -2222.93) * mm});
            skLineSegment(sketch, "E92", {"start": v(4592.32, -2222.93) * mm, "end": v(4592.32, -2143.66) * mm});
            skLineSegment(sketch, "E93", {"start": v(4592.32, -2143.66) * mm, "end": v(5008.88, -2143.66) * mm});
            skLineSegment(sketch, "E94", {"start": v(5008.88, -2143.66) * mm, "end": v(5008.88, -2222.93) * mm});
            skLineSegment(sketch, "E95", {"start": v(5008.88, -2222.93) * mm, "end": v(5059.68, -2222.93) * mm});
            skLineSegment(sketch, "E96", {"start": v(5059.68, -2222.93) * mm, "end": v(5059.68, -2143.66) * mm});
            skLineSegment(sketch, "E97", {"start": v(5059.68, -2143.66) * mm, "end": v(5476.24, -2143.66) * mm});
            skLineSegment(sketch, "E98", {"start": v(5476.24, -2143.66) * mm, "end": v(5476.24, -2222.93) * mm});
            skLineSegment(sketch, "E99", {"start": v(5476.24, -2222.93) * mm, "end": v(5527.04, -2222.93) * mm});
            skLineSegment(sketch, "E100", {"start": v(5527.04, -2222.93) * mm, "end": v(5527.04, -2143.66) * mm});
            skLineSegment(sketch, "E101", {"start": v(5527.04, -2143.66) * mm, "end": v(5943.6, -2143.66) * mm});
            skLineSegment(sketch, "E102", {"start": v(5943.6, -2143.66) * mm, "end": v(5943.6, -2222.93) * mm});
            skLineSegment(sketch, "E103", {"start": v(5943.6, -2222.93) * mm, "end": v(5918.2, -2222.93) * mm});
            skLineSegment(sketch, "E104", {"start": v(5918.2, -2222.93) * mm, "end": v(5918.2, -4331.13) * mm});
            skLineSegment(sketch, "E105", {"start": v(5918.2, -4331.13) * mm, "end": v(3683, -4331.13) * mm});
            skLineSegment(sketch, "E106", {"start": v(3683, -4331.13) * mm, "end": v(3683, -2222.93) * mm});
            skLineSegment(sketch, "E107", {"start": v(3683, -2222.93) * mm, "end": v(3657.6, -2222.93) * mm});
            skLineSegment(sketch, "E108", {"start": v(3657.6, -2222.93) * mm, "end": v(3657.6, -2143.66) * mm});
            skSolve(sketch);
        }
        {
            var Q0;
            Q0=makeQuery(id+"F59.imprint","IMPRINT",FACE,{"disambiguationData":[TD([[makeQuery(id+"F59.imprint","IMPRINT",EDGE,{"derivedFrom":sQuery(id+"F59.wireOp",EDGE,"E85")}),-1.0]])]});
            extrude(context, id + "F60", {"entities" : qUnion([Q0]), "depth" : 9 * mm});
        }
        {
            var Q0;
            Q0=makeQuery(id+"F60.opExtrude","CAP_FACE",FACE,{"disambiguationData":[OSD([sQuery(id+"F59.wireOp",EDGE,"E85"),sQuery(id+"F59.wireOp",EDGE,"E86"),sQuery(id+"F59.wireOp",EDGE,"E87"),sQuery(id+"F59.wireOp",EDGE,"E88"),sQuery(id+"F59.wireOp",EDGE,"E89"),sQuery(id+"F59.wireOp",EDGE,"E90"),sQuery(id+"F59.wireOp",EDGE,"E91"),sQuery(id+"F59.wireOp",EDGE,"E92"),sQuery(id+"F59.wireOp",EDGE,"E93"),sQuery(id+"F59.wireOp",EDGE,"E94"),sQuery(id+"F59.wireOp",EDGE,"E95"),sQuery(id+"F59.wireOp",EDGE,"E96"),sQuery(id+"F59.wireOp",EDGE,"E97"),sQuery(id+"F59.wireOp",EDGE,"E98"),sQuery(id+"F59.wireOp",EDGE,"E99"),sQuery(id+"F59.wireOp",EDGE,"E100"),sQuery(id+"F59.wireOp",EDGE,"E101"),sQuery(id+"F59.wireOp",EDGE,"E102"),sQuery(id+"F59.wireOp",EDGE,"E103"),sQuery(id+"F59.wireOp",EDGE,"E104"),sQuery(id+"F59.wireOp",EDGE,"E105"),sQuery(id+"F59.wireOp",EDGE,"E106"),sQuery(id+"F59.wireOp",EDGE,"E107"),sQuery(id+"F59.wireOp",EDGE,"E108")])],"isStart":false});
            var sketch = newSketch(context, id + "F61", { "sketchPlane" : qUnion([Q0])});
            skLineSegment(sketch, "E109.bottom", {"start": v(4038.6, -2702.35) * mm, "end": v(4648.2, -2702.35) * mm});
            skLineSegment(sketch, "E109.top", {"start": v(4038.6, -3616.75) * mm, "end": v(4648.2, -3616.75) * mm});
            skLineSegment(sketch, "E109.left", {"start": v(4038.6, -2702.35) * mm, "end": v(4038.6, -3616.75) * mm});
            skLineSegment(sketch, "E109.right", {"start": v(4648.2, -2702.35) * mm, "end": v(4648.2, -3616.75) * mm});
            skLineSegment(sketch, "E110.bottom", {"start": v(4953, -2702.35) * mm, "end": v(5562.6, -2702.35) * mm});
            skLineSegment(sketch, "E110.top", {"start": v(4953, -4305.73) * mm, "end": v(5562.6, -4305.73) * mm});
            skLineSegment(sketch, "E110.left", {"start": v(4953, -2702.35) * mm, "end": v(4953, -4305.73) * mm});
            skLineSegment(sketch, "E110.right", {"start": v(5562.6, -2702.35) * mm, "end": v(5562.6, -4305.73) * mm});
            skSolve(sketch);
        }
        {
            var Q0;
            Q0=makeQuery(id+"F61.imprint","IMPRINT",FACE,{"disambiguationData":[TD([[makeQuery(id+"F61.imprint","IMPRINT",EDGE,{"derivedFrom":sQuery(id+"F61.wireOp",EDGE,"E109.bottom")}),-1.0]])]});
            var Q1;
            Q1=makeQuery(id+"F61.imprint","IMPRINT",FACE,{"disambiguationData":[TD([[makeQuery(id+"F61.imprint","IMPRINT",EDGE,{"derivedFrom":sQuery(id+"F61.wireOp",EDGE,"E110.bottom")}),-1.0]])]});
            extrude(context, id + "F62", {"entities" : qUnion([Q0, Q1]), "operationType" : NewBodyOperationType.REMOVE, "endBound" : BoundingType.UP_TO_NEXT, "oppositeDirection" : true, "depth" : 25.4 * mm});
        }
        {
            var Q0;
            Q0=qCreatedBy(makeId("Top.planeOp"),FACE);
            var sketch = newSketch(context, id + "F63", { "sketchPlane" : qUnion([Q0])});
            skLineSegment(sketch, "E111.bottom", {"start": v(-368.27, 53.7) * mm, "end": v(-317.47, 53.7) * mm});
            skLineSegment(sketch, "E111.top", {"start": v(-368.27, 2.9) * mm, "end": v(-317.47, 2.9) * mm});
            skLineSegment(sketch, "E111.left", {"start": v(-368.27, 53.7) * mm, "end": v(-368.27, 2.9) * mm});
            skLineSegment(sketch, "E111.right", {"start": v(-317.47, 53.7) * mm, "end": v(-317.47, 2.9) * mm});
            skSolve(sketch);
        }
        {
            var Q0;
            Q0=makeQuery(id+"F63.imprint","IMPRINT",FACE,{"disambiguationData":[TD([[makeQuery(id+"F63.imprint","IMPRINT",EDGE,{"derivedFrom":sQuery(id+"F63.wireOp",EDGE,"E111.bottom")}),-1.0]])]});
            extrude(context, id + "F64", {"entities" : qUnion([Q0]), "depth" : 685.8 * mm});
        }
        {
            var Q0;
            Q0=qCreatedBy(makeId("Top.planeOp"),FACE);
            var sketch = newSketch(context, id + "F65", { "sketchPlane" : qUnion([Q0])});
            skLineSegment(sketch, "E112.bottom", {"start": v(-723.87, 50.8) * mm, "end": v(-622.27, 50.8) * mm});
            skLineSegment(sketch, "E112.top", {"start": v(-723.87, -50.8) * mm, "end": v(-622.27, -50.8) * mm});
            skLineSegment(sketch, "E112.left", {"start": v(-723.87, 50.8) * mm, "end": v(-723.87, -50.8) * mm});
            skLineSegment(sketch, "E112.right", {"start": v(-622.27, 50.8) * mm, "end": v(-622.27, -50.8) * mm});
            skSolve(sketch);
        }
        {
            var Q0;
            Q0=makeQuery(id+"F65.imprint","IMPRINT",FACE,{"disambiguationData":[TD([[makeQuery(id+"F65.imprint","IMPRINT",EDGE,{"derivedFrom":sQuery(id+"F65.wireOp",EDGE,"E112.bottom")}),-1.0]])]});
            extrude(context, id + "F66", {"entities" : qUnion([Q0]), "depth" : 762 * mm});
        }
    });
